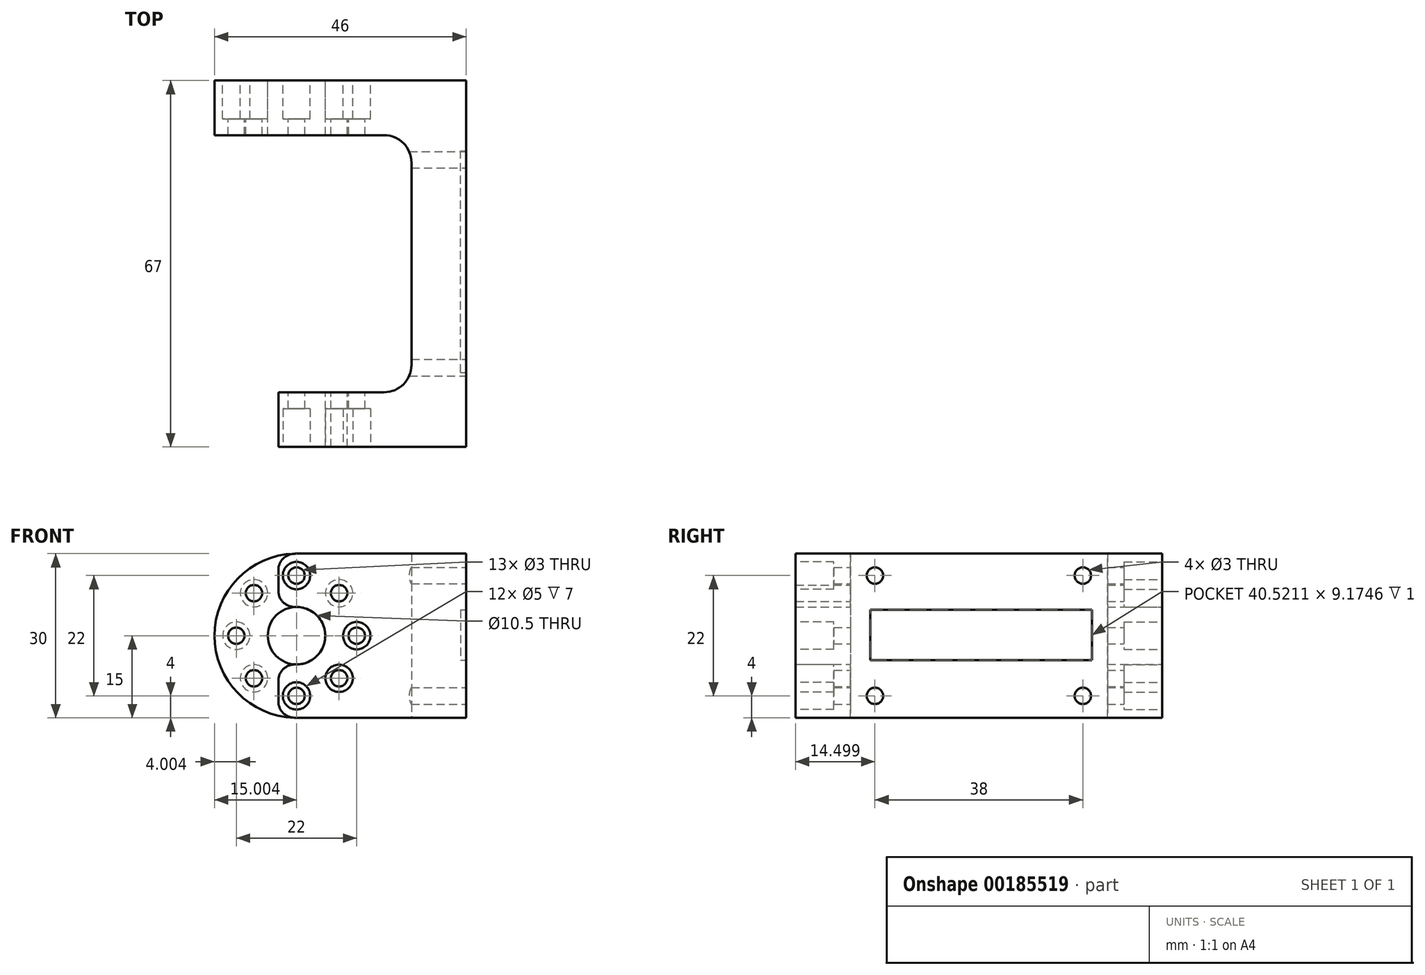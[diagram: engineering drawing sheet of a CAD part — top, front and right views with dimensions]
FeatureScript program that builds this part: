
annotation { "Feature Type Name" : "Feature", "Feature Type Description" : "" }
export const myFeature = defineFeature(function(context is Context, id is Id, definition is map)
    precondition{}
    {
        {
            var Q0;
            Q0=qCreatedBy(makeId("Top.planeOp"),FACE);
            var sketch = newSketch(context, id + "F0", { "sketchPlane" : qUnion([Q0])});
            skLineSegment(sketch, "E0.bottom", {"start": v(-19.49, 39.8) * mm, "end": v(26.51, 39.8) * mm});
            skLineSegment(sketch, "E0.top", {"start": v(-19.49, -27.2) * mm, "end": v(26.51, -27.2) * mm});
            skLineSegment(sketch, "E0.left", {"start": v(-19.49, 39.8) * mm, "end": v(-19.49, 29.8) * mm});
            skLineSegment(sketch, "E0.right", {"start": v(26.51, 39.8) * mm, "end": v(26.51, -27.2) * mm});
            skLineSegment(sketch, "E1.bottom", {"start": v(-19.49, 29.8) * mm, "end": v(16.51, 29.8) * mm});
            skLineSegment(sketch, "E1.top", {"start": v(-19.49, -17.2) * mm, "end": v(16.51, -17.2) * mm});
            skLineSegment(sketch, "E1.right", {"start": v(16.51, 29.8) * mm, "end": v(16.51, -17.2) * mm});
            skLineSegment(sketch, "E2.trimOffspring", {"start": v(-19.49, -17.2) * mm, "end": v(-19.49, -27.2) * mm});
            skSolve(sketch);
        }
        {
            var Q0;
            Q0 = qSketchRegion(id + "F0", true);
            extrude(context, id + "F1", {"entities" : qUnion([Q0]), "depth" : 30 * mm});
        }
        {
            var Q0;
            Q0=makeQuery(id+"F1.opExtrude","CAP_EDGE",EDGE,{"disambiguationData":[OSD([sQuery(id+"F0.wireOp",EDGE,"E0.left")])],"isStart":false});
            var Q1;
            Q1=makeQuery(id+"F1.opExtrude","CAP_EDGE",EDGE,{"disambiguationData":[OSD([sQuery(id+"F0.wireOp",EDGE,"E0.left")])],"isStart":true});
            var Q2;
            Q2=makeQuery(id+"F1.opExtrude","CAP_EDGE",EDGE,{"disambiguationData":[OSD([sQuery(id+"F0.wireOp",EDGE,"E2.trimOffspring")])],"isStart":false});
            var Q3;
            Q3=makeQuery(id+"F1.opExtrude","CAP_EDGE",EDGE,{"disambiguationData":[OSD([sQuery(id+"F0.wireOp",EDGE,"E2.trimOffspring")])],"isStart":true});
            fillet(context, id + "F2", {"entities" : qUnion([Q0, Q1, Q2, Q3]), "radius" : 15 * mm, "tangentPropagation" : true, "allowEdgeOverflow" : false});
        }
        {
            var Q0;
            Q0=makeQuery(id+"F1.opExtrude","SWEPT_FACE",FACE,{"disambiguationData":[OSD([sQuery(id+"F0.wireOp",EDGE,"E0.bottom")])]});
            var sketch = newSketch(context, id + "F3", { "sketchPlane" : qUnion([Q0])});
            skCircle(sketch, "E3", {"center": v(4.49, 15) * mm, "radius": 5.25 * mm});
            skSolve(sketch);
        }
        {
            var Q0;
            Q0=makeQuery(id+"F3.imprint","IMPRINT",FACE,{"disambiguationData":[TD([[makeQuery(id+"F3.imprint","IMPRINT",EDGE,{"derivedFrom":sQuery(id+"F3.wireOp",EDGE,"E3")}),1.0]])]});
            extrude(context, id + "F4", {"entities" : qUnion([Q0]), "operationType" : NewBodyOperationType.REMOVE, "oppositeDirection" : true, "depth" : 100 * mm});
        }
        {
            var Q0;
            Q0=makeQuery(id+"F1.opExtrude","SWEPT_FACE",FACE,{"disambiguationData":[OSD([sQuery(id+"F0.wireOp",EDGE,"E0.bottom")])]});
            var sketch = newSketch(context, id + "F5", { "sketchPlane" : qUnion([Q0])});
            skCircle(sketch, "E4", {"center": v(4.49, 26) * mm, "radius": 2.5 * mm});
            skCircle(sketch, "E5.1.0", {"center": v(-3.3, 22.78) * mm, "radius": 2.5 * mm});
            skCircle(sketch, "E5.2.0", {"center": v(-6.51, 15) * mm, "radius": 2.5 * mm});
            skCircle(sketch, "E5.3.0", {"center": v(-3.3, 7.22) * mm, "radius": 2.5 * mm});
            skCircle(sketch, "E5.4.0", {"center": v(4.49, 4) * mm, "radius": 2.5 * mm});
            skCircle(sketch, "E5.5.0", {"center": v(12.26, 7.22) * mm, "radius": 2.5 * mm});
            skCircle(sketch, "E5.6.0", {"center": v(15.49, 15) * mm, "radius": 2.5 * mm});
            skCircle(sketch, "E5.7.0", {"center": v(12.26, 22.78) * mm, "radius": 2.5 * mm});
            skPoint(sketch, "E5.center", {"position": v(4.49, 15) * mm});
            skSolve(sketch);
        }
        {
            var Q0;
            Q0=makeQuery(id+"F5.imprint","IMPRINT",FACE,{"disambiguationData":[TD([[makeQuery(id+"F5.imprint","IMPRINT",EDGE,{"derivedFrom":sQuery(id+"F5.wireOp",EDGE,"E4")}),1.0]])]});
            extrude(context, id + "F6", {"entities" : qUnion([Q0]), "operationType" : NewBodyOperationType.REMOVE, "oppositeDirection" : true, "depth" : 7 * mm});
        }
        {
            var Q0;
            Q0=makeQuery(id+"F5.imprint","IMPRINT",FACE,{"disambiguationData":[TD([[makeQuery(id+"F5.imprint","IMPRINT",EDGE,{"derivedFrom":sQuery(id+"F5.wireOp",EDGE,"E5.1.0")}),1.0]])]});
            var Q1;
            Q1=makeQuery(id+"F5.imprint","IMPRINT",FACE,{"disambiguationData":[TD([[makeQuery(id+"F5.imprint","IMPRINT",EDGE,{"derivedFrom":sQuery(id+"F5.wireOp",EDGE,"E5.2.0")}),1.0]])]});
            var Q2;
            Q2=makeQuery(id+"F5.imprint","IMPRINT",FACE,{"disambiguationData":[TD([[makeQuery(id+"F5.imprint","IMPRINT",EDGE,{"derivedFrom":sQuery(id+"F5.wireOp",EDGE,"E5.3.0")}),1.0]])]});
            var Q3;
            Q3=makeQuery(id+"F5.imprint","IMPRINT",FACE,{"disambiguationData":[TD([[makeQuery(id+"F5.imprint","IMPRINT",EDGE,{"derivedFrom":sQuery(id+"F5.wireOp",EDGE,"E5.4.0")}),1.0]])]});
            var Q4;
            Q4=makeQuery(id+"F5.imprint","IMPRINT",FACE,{"disambiguationData":[TD([[makeQuery(id+"F5.imprint","IMPRINT",EDGE,{"derivedFrom":sQuery(id+"F5.wireOp",EDGE,"E5.5.0")}),1.0]])]});
            var Q5;
            Q5=makeQuery(id+"F5.imprint","IMPRINT",FACE,{"disambiguationData":[TD([[makeQuery(id+"F5.imprint","IMPRINT",EDGE,{"derivedFrom":sQuery(id+"F5.wireOp",EDGE,"E5.6.0")}),1.0]])]});
            var Q6;
            Q6=makeQuery(id+"F5.imprint","IMPRINT",FACE,{"disambiguationData":[TD([[makeQuery(id+"F5.imprint","IMPRINT",EDGE,{"derivedFrom":sQuery(id+"F5.wireOp",EDGE,"E5.7.0")}),1.0]])]});
            extrude(context, id + "F7", {"entities" : qUnion([Q0, Q1, Q2, Q3, Q4, Q5, Q6]), "operationType" : NewBodyOperationType.REMOVE, "oppositeDirection" : true, "depth" : 7 * mm});
        }
        {
            var Q0;
            Q0=makeQuery(id+"F5.imprint","IMPRINT",FACE,{"disambiguationData":[TD([[makeQuery(id+"F5.imprint","IMPRINT",EDGE,{"derivedFrom":sQuery(id+"F5.wireOp",EDGE,"E4")}),-1.0]])]});
            var sketch = newSketch(context, id + "F8", { "sketchPlane" : qUnion([Q0])});
            skCircle(sketch, "E6", {"center": v(4.49, 26) * mm, "radius": 1.5 * mm});
            skCircle(sketch, "E7.0.0", {"center": v(4.49, 15) * mm, "radius": 5.25 * mm});
            skCircle(sketch, "E8.1.0", {"center": v(-3.3, 22.78) * mm, "radius": 1.5 * mm});
            skCircle(sketch, "E8.2.0", {"center": v(-6.51, 15) * mm, "radius": 1.5 * mm});
            skCircle(sketch, "E8.3.0", {"center": v(-3.3, 7.22) * mm, "radius": 1.5 * mm});
            skCircle(sketch, "E8.4.0", {"center": v(4.49, 4) * mm, "radius": 1.5 * mm});
            skCircle(sketch, "E8.5.0", {"center": v(12.26, 7.22) * mm, "radius": 1.5 * mm});
            skCircle(sketch, "E8.6.0", {"center": v(15.49, 15) * mm, "radius": 1.5 * mm});
            skCircle(sketch, "E8.7.0", {"center": v(12.26, 22.78) * mm, "radius": 1.5 * mm});
            skSolve(sketch);
        }
        {
            var Q0;
            Q0=makeQuery(id+"F8.imprint","IMPRINT",FACE,{"disambiguationData":[TD([[makeQuery(id+"F8.imprint","IMPRINT",EDGE,{"derivedFrom":sQuery(id+"F8.wireOp",EDGE,"E6")}),1.0]])]});
            var Q1;
            Q1=makeQuery(id+"F8.imprint","IMPRINT",FACE,{"disambiguationData":[TD([[makeQuery(id+"F8.imprint","IMPRINT",EDGE,{"derivedFrom":sQuery(id+"F8.wireOp",EDGE,"E8.7.0")}),1.0]])]});
            var Q2;
            Q2=makeQuery(id+"F8.imprint","IMPRINT",FACE,{"disambiguationData":[TD([[makeQuery(id+"F8.imprint","IMPRINT",EDGE,{"derivedFrom":sQuery(id+"F8.wireOp",EDGE,"E8.6.0")}),1.0]])]});
            var Q3;
            Q3=makeQuery(id+"F8.imprint","IMPRINT",FACE,{"disambiguationData":[TD([[makeQuery(id+"F8.imprint","IMPRINT",EDGE,{"derivedFrom":sQuery(id+"F8.wireOp",EDGE,"E8.5.0")}),1.0]])]});
            var Q4;
            Q4=makeQuery(id+"F8.imprint","IMPRINT",FACE,{"disambiguationData":[TD([[makeQuery(id+"F8.imprint","IMPRINT",EDGE,{"derivedFrom":sQuery(id+"F8.wireOp",EDGE,"E8.4.0")}),1.0]])]});
            var Q5;
            Q5=makeQuery(id+"F8.imprint","IMPRINT",FACE,{"disambiguationData":[TD([[makeQuery(id+"F8.imprint","IMPRINT",EDGE,{"derivedFrom":sQuery(id+"F8.wireOp",EDGE,"E8.3.0")}),1.0]])]});
            var Q6;
            Q6=makeQuery(id+"F8.imprint","IMPRINT",FACE,{"disambiguationData":[TD([[makeQuery(id+"F8.imprint","IMPRINT",EDGE,{"derivedFrom":sQuery(id+"F8.wireOp",EDGE,"E8.2.0")}),1.0]])]});
            var Q7;
            Q7=makeQuery(id+"F8.imprint","IMPRINT",FACE,{"disambiguationData":[TD([[makeQuery(id+"F8.imprint","IMPRINT",EDGE,{"derivedFrom":sQuery(id+"F8.wireOp",EDGE,"E8.1.0")}),1.0]])]});
            extrude(context, id + "F9", {"entities" : qUnion([Q0, Q1, Q2, Q3, Q4, Q5, Q6, Q7]), "operationType" : NewBodyOperationType.REMOVE, "oppositeDirection" : true, "depth" : 100 * mm});
        }
        {
            var Q0;
            Q0=makeQuery(id+"F1.opExtrude","SWEPT_FACE",FACE,{"disambiguationData":[OSD([sQuery(id+"F0.wireOp",EDGE,"E0.top")])]});
            var sketch = newSketch(context, id + "F10", { "sketchPlane" : qUnion([Q0])});
            skCircle(sketch, "E9.0", {"center": v(-4.49, 15) * mm, "radius": 5.25 * mm});
            skCircle(sketch, "E10.0", {"center": v(-4.49, 26) * mm, "radius": 1.5 * mm});
            skCircle(sketch, "E11", {"center": v(-4.49, 26) * mm, "radius": 2.5 * mm});
            skCircle(sketch, "E12.1.0", {"center": v(-12.26, 22.78) * mm, "radius": 2.5 * mm});
            skCircle(sketch, "E12.2.0", {"center": v(-15.49, 15) * mm, "radius": 2.5 * mm});
            skCircle(sketch, "E12.3.0", {"center": v(-12.26, 7.22) * mm, "radius": 2.5 * mm});
            skCircle(sketch, "E12.4.0", {"center": v(-4.49, 4) * mm, "radius": 2.5 * mm});
            skCircle(sketch, "E12.5.0", {"center": v(3.3, 7.22) * mm, "radius": 2.5 * mm});
            skCircle(sketch, "E12.6.0", {"center": v(6.51, 15) * mm, "radius": 2.5 * mm});
            skCircle(sketch, "E12.7.0", {"center": v(3.3, 22.78) * mm, "radius": 2.5 * mm});
            skSolve(sketch);
        }
        {
            var Q0;
            Q0=makeQuery(id+"F10.imprint","IMPRINT",FACE,{"disambiguationData":[TD([[makeQuery(id+"F10.imprint","IMPRINT",EDGE,{"derivedFrom":sQuery(id+"F10.wireOp",EDGE,"E10.0")}),1.0]])]});
            var Q1;
            Q1=makeQuery(id+"F10.imprint","IMPRINT",FACE,{"disambiguationData":[TD([[makeQuery(id+"F10.imprint","IMPRINT",EDGE,{"derivedFrom":sQuery(id+"F10.wireOp",EDGE,"E12.1.0")}),1.0]])]});
            var Q2;
            Q2=makeQuery(id+"F10.imprint","IMPRINT",FACE,{"disambiguationData":[TD([[makeQuery(id+"F10.imprint","IMPRINT",EDGE,{"derivedFrom":sQuery(id+"F10.wireOp",EDGE,"E12.2.0")}),1.0]])]});
            var Q3;
            Q3=makeQuery(id+"F10.imprint","IMPRINT",FACE,{"disambiguationData":[TD([[makeQuery(id+"F10.imprint","IMPRINT",EDGE,{"derivedFrom":sQuery(id+"F10.wireOp",EDGE,"E12.3.0")}),1.0]])]});
            var Q4;
            Q4=makeQuery(id+"F10.imprint","IMPRINT",FACE,{"disambiguationData":[TD([[makeQuery(id+"F10.imprint","IMPRINT",EDGE,{"derivedFrom":sQuery(id+"F10.wireOp",EDGE,"E12.4.0")}),1.0]])]});
            var Q5;
            Q5=makeQuery(id+"F10.imprint","IMPRINT",FACE,{"disambiguationData":[TD([[makeQuery(id+"F10.imprint","IMPRINT",EDGE,{"derivedFrom":sQuery(id+"F10.wireOp",EDGE,"E12.5.0")}),1.0]])]});
            var Q6;
            Q6=makeQuery(id+"F10.imprint","IMPRINT",FACE,{"disambiguationData":[TD([[makeQuery(id+"F10.imprint","IMPRINT",EDGE,{"derivedFrom":sQuery(id+"F10.wireOp",EDGE,"E12.6.0")}),1.0]])]});
            extrude(context, id + "F11", {"entities" : qUnion([Q0, Q1, Q2, Q3, Q4, Q5, Q6]), "operationType" : NewBodyOperationType.REMOVE, "oppositeDirection" : true, "depth" : 7 * mm});
        }
        {
            var Q0;
            Q0=makeQuery(id+"F1.opExtrude","SWEPT_FACE",FACE,{"disambiguationData":[OSD([sQuery(id+"F0.wireOp",EDGE,"E0.top")])]});
            var sketch = newSketch(context, id + "F12", { "sketchPlane" : qUnion([Q0])});
            skLineSegment(sketch, "E13.bottom", {"start": v(-27.56, 34.15) * mm, "end": v(-7.81, 34.15) * mm});
            skLineSegment(sketch, "E13.top", {"start": v(-27.56, -2.42) * mm, "end": v(-7.81, -2.42) * mm});
            skLineSegment(sketch, "E13.left", {"start": v(-27.56, 34.15) * mm, "end": v(-27.56, -2.42) * mm});
            skLineSegment(sketch, "E13.right", {"start": v(-7.81, 34.15) * mm, "end": v(-7.81, -2.42) * mm});
            skSolve(sketch);
        }
        {
            var Q0;
            Q0 = qSketchRegion(id + "F12", true);
            extrude(context, id + "F13", {"entities" : qUnion([Q0]), "operationType" : NewBodyOperationType.REMOVE, "oppositeDirection" : true, "depth" : 25 * mm});
        }
        {
            var Q0;
            Q0=makeQuery(id+"F13.boolean.opBoolean","INTERSECT",EDGE,{"disambiguationData":[OD(1.0)],"derivedFrom":[makeQuery(id+"F2.opFillet","BLEND_FACE",FACE,{"disambiguationData":[OSD([sQuery(id+"F0.wireOp",EDGE,"E2.trimOffspring")])]}),makeQuery(id+"F13.opExtrude","SWEPT_FACE",FACE,{"disambiguationData":[OSD([sQuery(id+"F12.wireOp",EDGE,"E13.right")])]})]});
            var Q1;
            Q1=makeQuery(id+"F13.boolean.opBoolean","INTERSECT",EDGE,{"disambiguationData":[OD(1.0)],"derivedFrom":[makeQuery(id+"F4.boolean.opBoolean","COPY",FACE,{"disambiguationData":[TD([makeQuery(id+"F1.opExtrude","SWEPT_FACE",FACE,{"disambiguationData":[OSD([sQuery(id+"F0.wireOp",EDGE,"E0.top")])]})])],"derivedFrom":makeQuery(id+"F4.opExtrude","SWEPT_FACE",FACE,{"disambiguationData":[OSD([sQuery(id+"F3.wireOp",EDGE,"E3")])]})}),makeQuery(id+"F13.opExtrude","SWEPT_FACE",FACE,{"disambiguationData":[OSD([sQuery(id+"F12.wireOp",EDGE,"E13.right")])]})]});
            var Q2;
            Q2=makeQuery(id+"F13.boolean.opBoolean","INTERSECT",EDGE,{"disambiguationData":[OD(0.0)],"derivedFrom":[makeQuery(id+"F4.boolean.opBoolean","COPY",FACE,{"disambiguationData":[TD([makeQuery(id+"F1.opExtrude","SWEPT_FACE",FACE,{"disambiguationData":[OSD([sQuery(id+"F0.wireOp",EDGE,"E0.top")])]})])],"derivedFrom":makeQuery(id+"F4.opExtrude","SWEPT_FACE",FACE,{"disambiguationData":[OSD([sQuery(id+"F3.wireOp",EDGE,"E3")])]})}),makeQuery(id+"F13.opExtrude","SWEPT_FACE",FACE,{"disambiguationData":[OSD([sQuery(id+"F12.wireOp",EDGE,"E13.right")])]})]});
            var Q3;
            Q3=makeQuery(id+"F13.boolean.opBoolean","INTERSECT",EDGE,{"disambiguationData":[OD(0.0)],"derivedFrom":[makeQuery(id+"F2.opFillet","BLEND_FACE",FACE,{"disambiguationData":[OSD([sQuery(id+"F0.wireOp",EDGE,"E2.trimOffspring")])]}),makeQuery(id+"F13.opExtrude","SWEPT_FACE",FACE,{"disambiguationData":[OSD([sQuery(id+"F12.wireOp",EDGE,"E13.right")])]})]});
            fillet(context, id + "F14", {"entities" : qUnion([Q0, Q1, Q2, Q3]), "radius" : 3 * mm, "tangentPropagation" : true, "allowEdgeOverflow" : false});
        }
        {
            var Q0;
            Q0=makeQuery(id+"F1.opExtrude","SWEPT_EDGE",EDGE,{"disambiguationData":[OSD([sQuery(id+"F0.wireOp",EDGE,"E1.bottom"),sQuery(id+"F0.wireOp",EDGE,"E1.right")])]});
            var Q1;
            Q1=makeQuery(id+"F1.opExtrude","SWEPT_EDGE",EDGE,{"disambiguationData":[OSD([sQuery(id+"F0.wireOp",EDGE,"E1.top"),sQuery(id+"F0.wireOp",EDGE,"E1.right")])]});
            fillet(context, id + "F15", {"entities" : qUnion([Q0, Q1]), "radius" : 5 * mm, "tangentPropagation" : true, "allowEdgeOverflow" : false});
        }
        {
            var Q0;
            Q0=makeQuery(id+"F1.opExtrude","SWEPT_FACE",FACE,{"disambiguationData":[OSD([sQuery(id+"F0.wireOp",EDGE,"E0.right")])]});
            var sketch = newSketch(context, id + "F16", { "sketchPlane" : qUnion([Q0])});
            skLineSegment(sketch, "E14.bottom", {"start": v(-12.7, 26) * mm, "end": v(25.3, 26) * mm, "construction": true});
            skLineSegment(sketch, "E14.top", {"start": v(-12.7, 4) * mm, "end": v(25.3, 4) * mm, "construction": true});
            skLineSegment(sketch, "E14.left", {"start": v(-12.7, 26) * mm, "end": v(-12.7, 4) * mm, "construction": true});
            skLineSegment(sketch, "E14.right", {"start": v(25.3, 26) * mm, "end": v(25.3, 4) * mm, "construction": true});
            skCircle(sketch, "E15", {"center": v(-12.7, 26) * mm, "radius": 1.5 * mm});
            skCircle(sketch, "E16", {"center": v(-12.7, 4) * mm, "radius": 1.5 * mm});
            skCircle(sketch, "E17", {"center": v(25.3, 4) * mm, "radius": 1.5 * mm});
            skCircle(sketch, "E18", {"center": v(25.3, 26) * mm, "radius": 1.5 * mm});
            skSolve(sketch);
        }
        {
            var Q0;
            Q0 = qSketchRegion(id + "F16", true);
            extrude(context, id + "F17", {"entities" : qUnion([Q0]), "operationType" : NewBodyOperationType.REMOVE, "oppositeDirection" : true, "depth" : 25 * mm});
        }
        {
            var Q0;
            Q0=makeQuery(id+"F1.opExtrude","SWEPT_FACE",FACE,{"disambiguationData":[OSD([sQuery(id+"F0.wireOp",EDGE,"E0.right")])]});
            var sketch = newSketch(context, id + "F18", { "sketchPlane" : qUnion([Q0])});
            skLineSegment(sketch, "E19.bottom", {"start": v(-13.57, 19.72) * mm, "end": v(26.95, 19.72) * mm});
            skLineSegment(sketch, "E19.top", {"start": v(-13.57, 10.55) * mm, "end": v(26.95, 10.55) * mm});
            skLineSegment(sketch, "E19.left", {"start": v(-13.57, 19.72) * mm, "end": v(-13.57, 10.55) * mm});
            skLineSegment(sketch, "E19.right", {"start": v(26.95, 19.72) * mm, "end": v(26.95, 10.55) * mm});
            skSolve(sketch);
        }
        {
            var Q0;
            Q0 = qSketchRegion(id + "F18", true);
            extrude(context, id + "F19", {"entities" : qUnion([Q0]), "operationType" : NewBodyOperationType.REMOVE, "oppositeDirection" : true, "depth" : 1 * mm});
        }
    });
